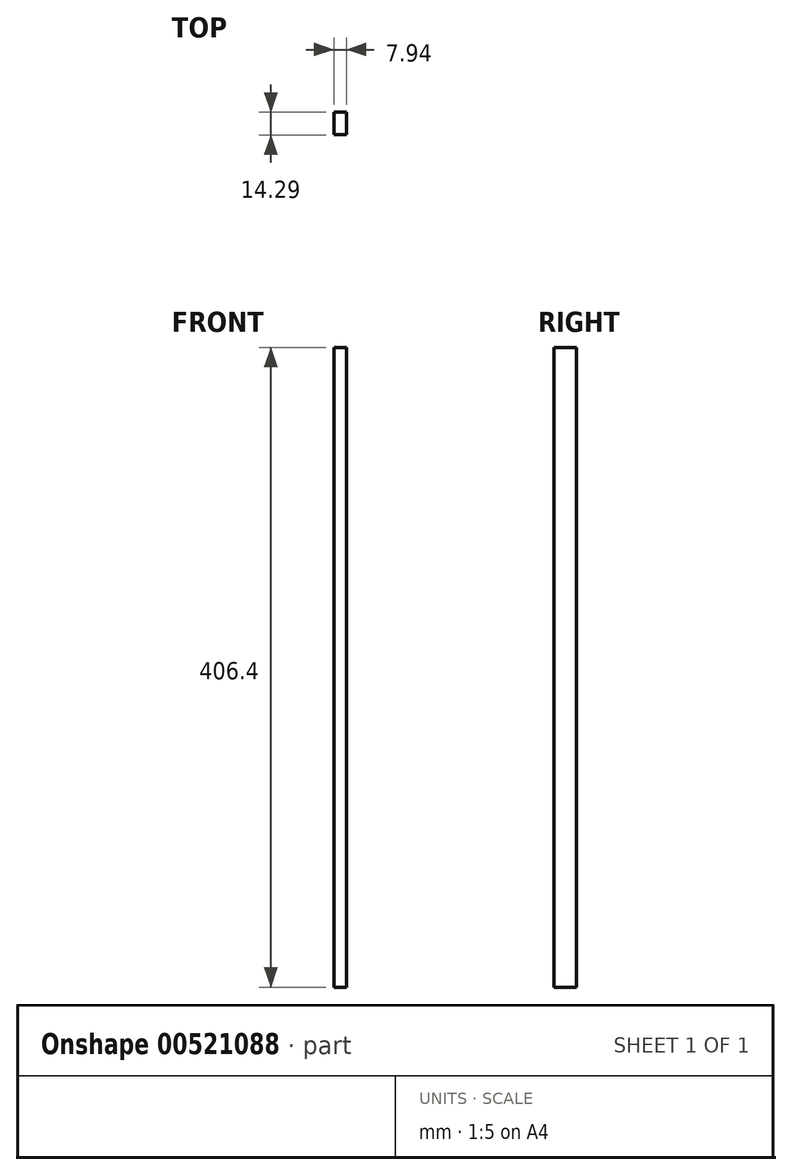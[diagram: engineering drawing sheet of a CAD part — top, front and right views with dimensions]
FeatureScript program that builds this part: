
annotation { "Feature Type Name" : "Feature", "Feature Type Description" : "" }
export const myFeature = defineFeature(function(context is Context, id is Id, definition is map)
    precondition{}
    {
        {
            var Q0;
            Q0=qCreatedBy(makeId("Top.planeOp"),FACE);
            var sketch = newSketch(context, id + "F0", { "sketchPlane" : qUnion([Q0])});
            skLineSegment(sketch, "E0", {"start": v(0, 84.2) * mm, "end": v(0, -97.88) * mm, "construction": true});
            skLineSegment(sketch, "E1", {"start": v(-103.43, 0) * mm, "end": v(103, 0) * mm, "construction": true});
            skLineSegment(sketch, "E2.bottom", {"start": v(-22.22, 57.15) * mm, "end": v(22.22, 57.15) * mm});
            skLineSegment(sketch, "E2.top", {"start": v(-22.22, -57.15) * mm, "end": v(22.23, -57.15) * mm});
            skLineSegment(sketch, "E2.left", {"start": v(-22.22, 57.15) * mm, "end": v(-22.22, -57.15) * mm});
            skLineSegment(sketch, "E2.right", {"start": v(22.23, 57.15) * mm, "end": v(22.23, -57.15) * mm});
            skLineSegment(sketch, "E3", {"start": v(14.29, 57.15) * mm, "end": v(14.29, -57.15) * mm, "construction": true});
            skLineSegment(sketch, "E4.bottom", {"start": v(22.22, 57.15) * mm, "end": v(14.29, 57.15) * mm});
            skLineSegment(sketch, "E4.top", {"start": v(22.23, 42.86) * mm, "end": v(14.29, 42.86) * mm});
            skLineSegment(sketch, "E4.left", {"start": v(22.22, 57.15) * mm, "end": v(22.22, 42.86) * mm});
            skLineSegment(sketch, "E4.right", {"start": v(14.29, 57.15) * mm, "end": v(14.29, 42.86) * mm});
            skLineSegment(sketch, "E5.0.1.0", {"start": v(22.23, 14.29) * mm, "end": v(14.29, 14.29) * mm});
            skLineSegment(sketch, "E5.0.1.1", {"start": v(14.29, 28.58) * mm, "end": v(14.29, 14.29) * mm});
            skLineSegment(sketch, "E5.0.1.2", {"start": v(22.22, 28.58) * mm, "end": v(14.29, 28.58) * mm});
            skLineSegment(sketch, "E5.0.2.0", {"start": v(22.23, -14.29) * mm, "end": v(14.29, -14.29) * mm});
            skLineSegment(sketch, "E5.0.2.1", {"start": v(14.29, 0) * mm, "end": v(14.29, -14.29) * mm});
            skLineSegment(sketch, "E5.0.2.2", {"start": v(22.22, 0) * mm, "end": v(14.29, 0) * mm});
            skLineSegment(sketch, "E5.0.3.0", {"start": v(22.23, -42.86) * mm, "end": v(14.29, -42.86) * mm});
            skLineSegment(sketch, "E5.0.3.1", {"start": v(14.29, -28.58) * mm, "end": v(14.29, -42.86) * mm});
            skLineSegment(sketch, "E5.0.3.2", {"start": v(22.22, -28.58) * mm, "end": v(14.29, -28.58) * mm});
            skLineSegment(sketch, "E5.direction1", {"start": v(14.29, 42.86) * mm, "end": v(39.69, 42.86) * mm, "construction": true});
            skLineSegment(sketch, "E5.direction2", {"start": v(14.29, 42.86) * mm, "end": v(14.29, 14.29) * mm, "construction": true});
            skSolve(sketch);
        }
        {
            var Q0;
            Q0=makeQuery(id+"F0.imprint","IMPRINT",FACE,{"disambiguationData":[TD([[makeQuery(id+"F0.imprint","IMPRINT",EDGE,{"derivedFrom":sQuery(id+"F0.wireOp",EDGE,"E2.bottom")}),-1.0]])]});
            extrude(context, id + "F1", {"entities" : qUnion([Q0]), "endBound" : BoundingType.SYMMETRIC, "depth" : 406.4 * mm, "offsetDistance" : 25.4 * mm});
        }
        {
            var Q0;
            {var subQ0=sQuery(id+"F0.wireOp",EDGE,"E2.right");Q0=makeQuery(id+"F1.opExtrude","SWEPT_FACE",FACE,{"disambiguationData":[OSD([subQ0]),TDD([makeQuery(id+"F0.imprint","IMPRINT",EDGE,{"disambiguationData":[TD([[makeQuery(id+"F0.imprint","INTERSECT",VERTEX,{"derivedFrom":[subQ0,sQuery(id+"F0.wireOp",EDGE,"E5.0.2.0")]}),-1.0]])],"derivedFrom":subQ0})])]});}
            var sketch = newSketch(context, id + "F2", { "sketchPlane" : qUnion([Q0])});
            skLineSegment(sketch, "E6.0.0", {"start": v(-28.58, -203.2) * mm, "end": v(-14.29, -203.2) * mm});
            skLineSegment(sketch, "E6.0.1", {"start": v(-14.29, -203.2) * mm, "end": v(-14.29, 203.2) * mm});
            skLineSegment(sketch, "E6.0.2", {"start": v(-14.29, 203.2) * mm, "end": v(-28.58, 203.2) * mm});
            skLineSegment(sketch, "E6.0.3", {"start": v(-28.58, 203.2) * mm, "end": v(-28.58, -203.2) * mm});
            skLineSegment(sketch, "E7", {"start": v(-21.43, 203.2) * mm, "end": v(-21.43, -203.2) * mm, "construction": true});
            skCircle(sketch, "E8", {"center": v(-21.43, 88.9) * mm, "radius": 5.56 * mm});
            skCircle(sketch, "E9", {"center": v(-21.43, 57.15) * mm, "radius": 5.56 * mm});
            skSolve(sketch);
        }
        {
            var Q0;
            Q0=makeQuery(id+"F2.imprint","IMPRINT",FACE,{"disambiguationData":[TD([[makeQuery(id+"F2.imprint","IMPRINT",EDGE,{"derivedFrom":sQuery(id+"F2.wireOp",EDGE,"E8")}),1.0]])]});
            var Q1;
            Q1=makeQuery(id+"F2.imprint","IMPRINT",FACE,{"disambiguationData":[TD([[makeQuery(id+"F2.imprint","IMPRINT",EDGE,{"derivedFrom":sQuery(id+"F2.wireOp",EDGE,"E9")}),1.0]])]});
            extrude(context, id + "F3", {"entities" : qUnion([Q0, Q1]), "operationType" : NewBodyOperationType.REMOVE, "endBound" : BoundingType.THROUGH_ALL, "oppositeDirection" : true, "depth" : 25.4 * mm, "offsetDistance" : 25.4 * mm});
        }
        {
            var Q0;
            Q0=makeQuery(id+"F1.opExtrude","CAP_FACE",FACE,{"disambiguationData":[OSD([sQuery(id+"F0.wireOp",EDGE,"E2.bottom"),sQuery(id+"F0.wireOp",EDGE,"E2.top"),sQuery(id+"F0.wireOp",EDGE,"E2.left"),sQuery(id+"F0.wireOp",EDGE,"E2.right"),sQuery(id+"F0.wireOp",EDGE,"E4.top"),sQuery(id+"F0.wireOp",EDGE,"E4.right"),sQuery(id+"F0.wireOp",EDGE,"E5.0.1.0"),sQuery(id+"F0.wireOp",EDGE,"E5.0.1.1"),sQuery(id+"F0.wireOp",EDGE,"E5.0.1.2"),sQuery(id+"F0.wireOp",EDGE,"E5.0.2.0"),sQuery(id+"F0.wireOp",EDGE,"E5.0.2.1"),sQuery(id+"F0.wireOp",EDGE,"E5.0.2.2"),sQuery(id+"F0.wireOp",EDGE,"E5.0.3.0"),sQuery(id+"F0.wireOp",EDGE,"E5.0.3.1"),sQuery(id+"F0.wireOp",EDGE,"E5.0.3.2")])],"isStart":true});
            var sketch = newSketch(context, id + "F4", { "sketchPlane" : qUnion([Q0])});
            skLineSegment(sketch, "E10", {"start": v(-3.17, 57.15) * mm, "end": v(-3.17, -57.15) * mm, "construction": true});
            skCircle(sketch, "E11", {"center": v(-3.17, 38.1) * mm, "radius": 9.53 * mm});
            skCircle(sketch, "E12", {"center": v(-3.17, -38.1) * mm, "radius": 9.53 * mm});
            skLineSegment(sketch, "E13", {"start": v(-73.86, 0) * mm, "end": v(77.24, 0) * mm, "construction": true});
            skSolve(sketch);
        }
        {
            var Q0;
            Q0=makeQuery(id+"F4.imprint","IMPRINT",FACE,{"disambiguationData":[TD([[makeQuery(id+"F4.imprint","IMPRINT",EDGE,{"derivedFrom":sQuery(id+"F4.wireOp",EDGE,"E12")}),1.0]])]});
            var Q1;
            Q1=makeQuery(id+"F4.imprint","IMPRINT",FACE,{"disambiguationData":[TD([[makeQuery(id+"F4.imprint","IMPRINT",EDGE,{"derivedFrom":sQuery(id+"F4.wireOp",EDGE,"E11")}),1.0]])]});
            extrude(context, id + "F5", {"entities" : qUnion([Q0, Q1]), "operationType" : NewBodyOperationType.REMOVE, "oppositeDirection" : true, "depth" : 76.2 * mm, "offsetDistance" : 25.4 * mm});
        }
    });
